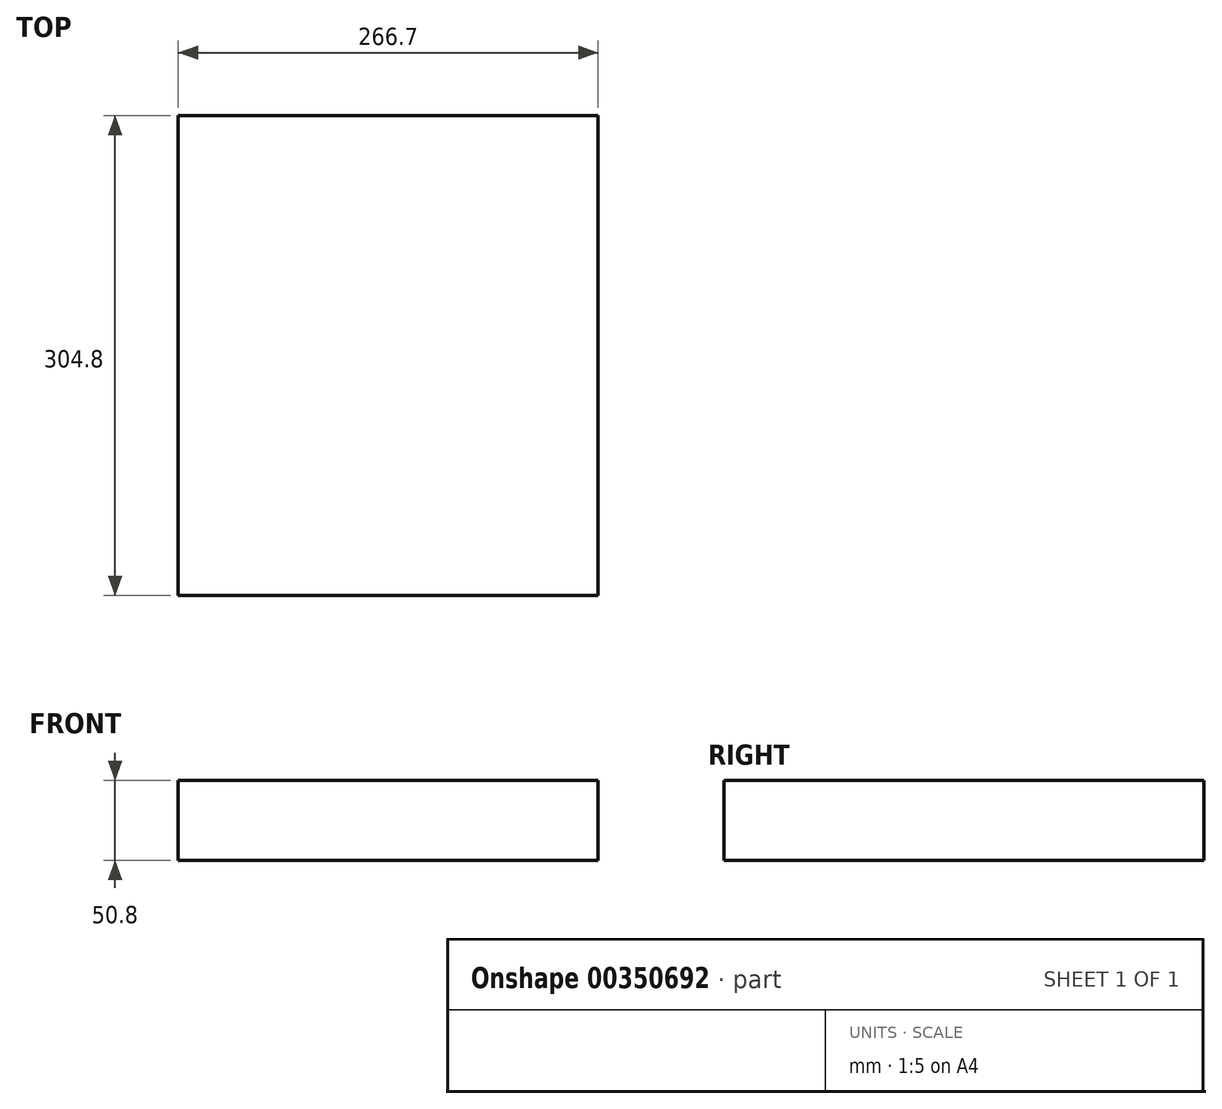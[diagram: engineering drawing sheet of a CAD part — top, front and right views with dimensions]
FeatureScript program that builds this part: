
annotation { "Feature Type Name" : "Feature", "Feature Type Description" : "" }
export const myFeature = defineFeature(function(context is Context, id is Id, definition is map)
    precondition{}
    {
        {
            var Q0;
            Q0=qCreatedBy(makeId("Front.planeOp"),FACE);
            var sketch = newSketch(context, id + "F0", { "sketchPlane" : qUnion([Q0])});
            skLineSegment(sketch, "E0.bottom", {"start": v(-133.35, 25.4) * mm, "end": v(133.35, 25.4) * mm});
            skLineSegment(sketch, "E0.top", {"start": v(-133.35, -25.4) * mm, "end": v(133.35, -25.4) * mm});
            skLineSegment(sketch, "E0.left", {"start": v(-133.35, 25.4) * mm, "end": v(-133.35, -25.4) * mm});
            skLineSegment(sketch, "E0.right", {"start": v(133.35, 25.4) * mm, "end": v(133.35, -25.4) * mm});
            skPoint(sketch, "E0.middle", {"position": v(0, 0) * mm});
            skSolve(sketch);
        }
        {
            var Q0;
            Q0=makeQuery(id+"F0.imprint","IMPRINT",FACE,{"disambiguationData":[TD([[makeQuery(id+"F0.imprint","IMPRINT",EDGE,{"derivedFrom":sQuery(id+"F0.wireOp",EDGE,"E0.bottom")}),-1.0]])]});
            extrude(context, id + "F1", {"entities" : qUnion([Q0]), "oppositeDirection" : true, "depth" : 304.8 * mm});
        }
    });
